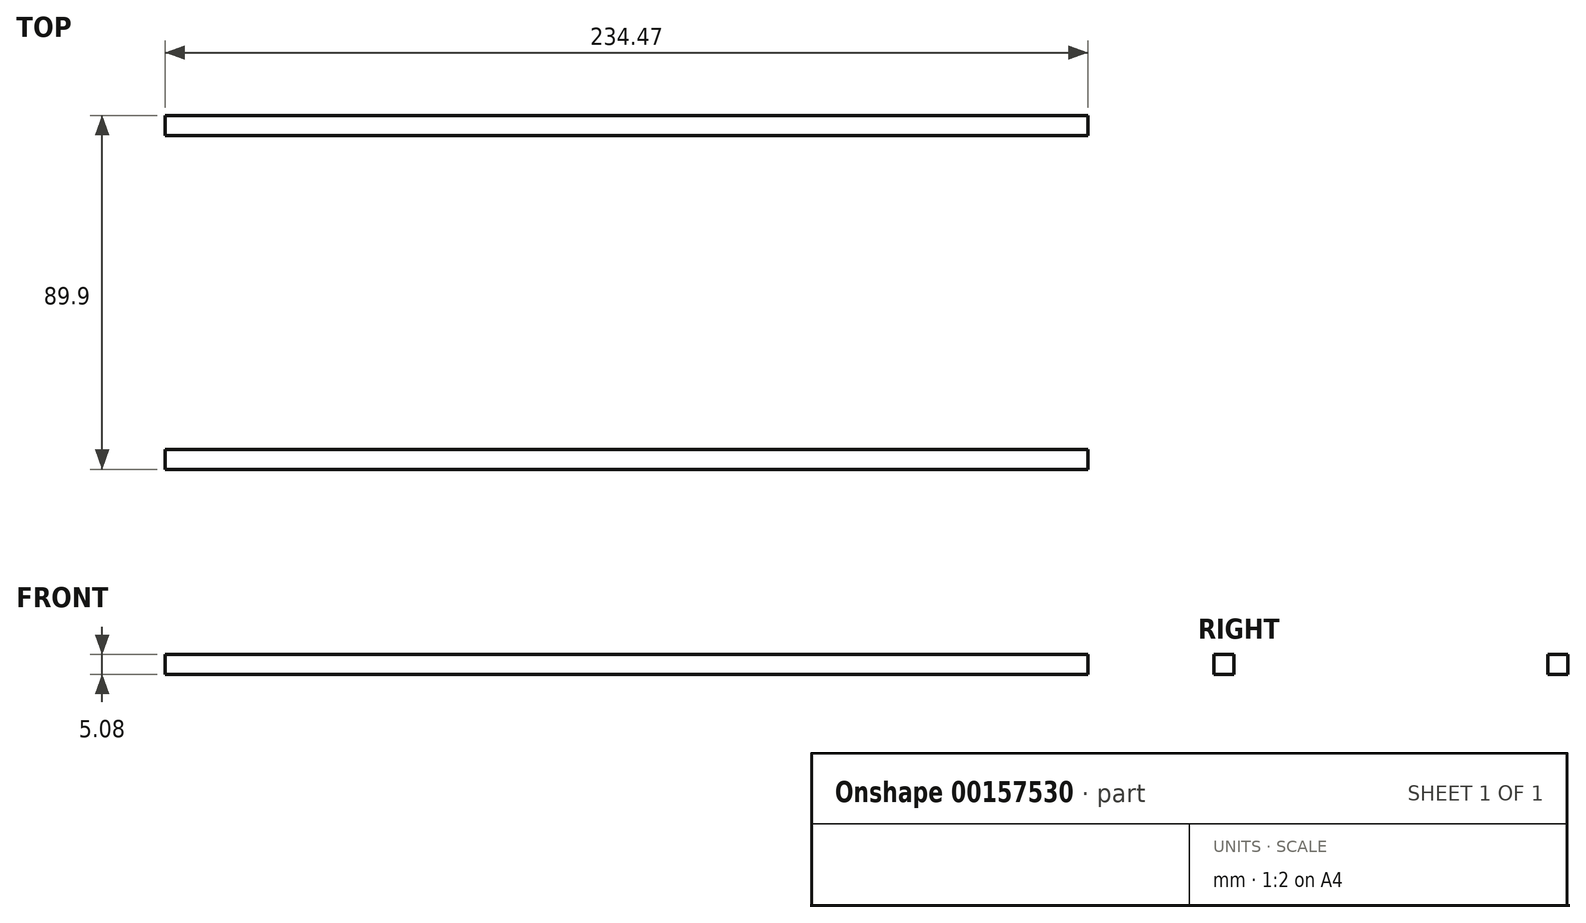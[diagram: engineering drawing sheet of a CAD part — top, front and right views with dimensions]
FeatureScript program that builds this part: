
annotation { "Feature Type Name" : "Feature", "Feature Type Description" : "" }
export const myFeature = defineFeature(function(context is Context, id is Id, definition is map)
    precondition{}
    {
        {
            var Q0;
            Q0=qCreatedBy(makeId("Top.planeOp"),FACE);
            var sketch = newSketch(context, id + "F0", { "sketchPlane" : qUnion([Q0])});
            skLineSegment(sketch, "E0.bottom", {"start": v(-142.14, -41) * mm, "end": v(92.33, -41) * mm});
            skLineSegment(sketch, "E0.top", {"start": v(-142.14, -46.08) * mm, "end": v(92.33, -46.08) * mm});
            skLineSegment(sketch, "E0.left", {"start": v(-142.14, -41) * mm, "end": v(-142.14, -46.08) * mm});
            skLineSegment(sketch, "E0.right", {"start": v(92.33, -41) * mm, "end": v(92.33, -46.08) * mm});
            skLineSegment(sketch, "E1.bottom", {"start": v(92.33, 43.82) * mm, "end": v(-142.14, 43.82) * mm});
            skLineSegment(sketch, "E1.top", {"start": v(92.33, 38.73) * mm, "end": v(-142.14, 38.73) * mm});
            skLineSegment(sketch, "E1.left", {"start": v(92.33, 43.82) * mm, "end": v(92.33, 38.73) * mm});
            skLineSegment(sketch, "E1.right", {"start": v(-142.14, 43.82) * mm, "end": v(-142.14, 38.73) * mm});
            skSolve(sketch);
        }
        {
            var Q0;
            Q0=makeQuery(id+"F0.imprint","IMPRINT",FACE,{"disambiguationData":[TD([[makeQuery(id+"F0.imprint","IMPRINT",EDGE,{"derivedFrom":sQuery(id+"F0.wireOp",EDGE,"E0.bottom")}),-1.0]])]});
            var Q1;
            Q1=makeQuery(id+"F0.imprint","IMPRINT",FACE,{"disambiguationData":[TD([[makeQuery(id+"F0.imprint","IMPRINT",EDGE,{"derivedFrom":sQuery(id+"F0.wireOp",EDGE,"E1.bottom")}),1.0]])]});
            extrude(context, id + "F1", {"entities" : qUnion([Q0, Q1]), "depth" : 5.08 * mm});
        }
    });
